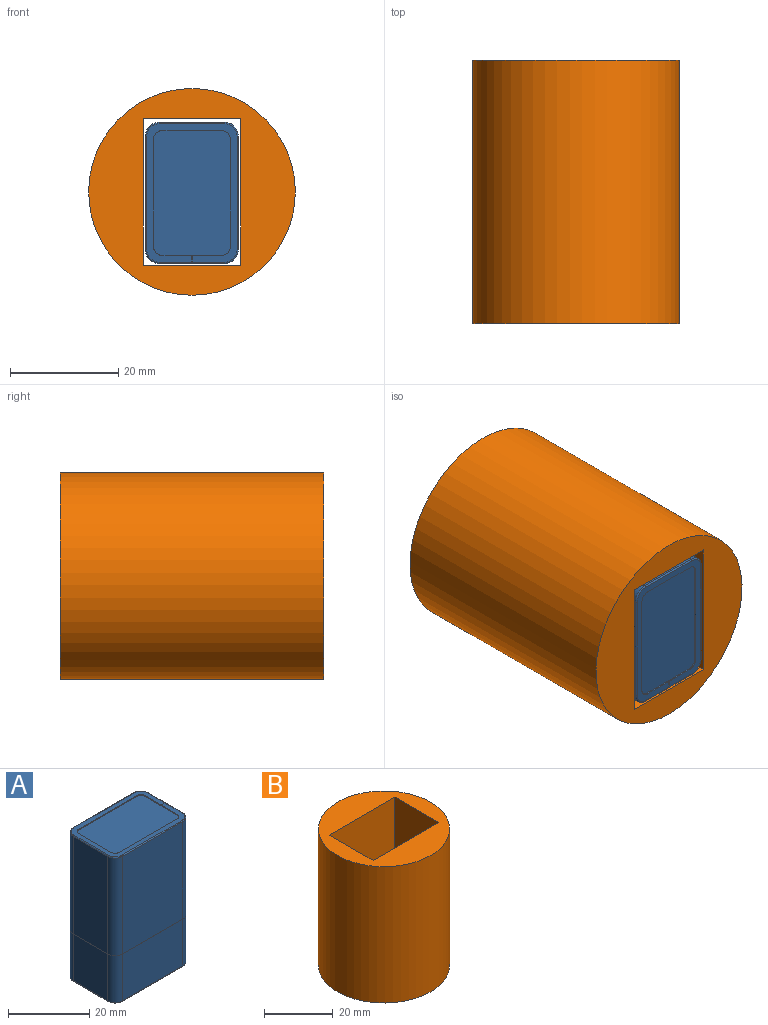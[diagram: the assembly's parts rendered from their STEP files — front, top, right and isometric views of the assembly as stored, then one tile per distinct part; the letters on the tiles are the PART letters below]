
ASSEMBLY  parts=2 mates=1
PART A: 190 faces, bbox 26.5x17.6x47.9 mm
  f0: cylinder r=0.25mm len=20.96mm, axis (1,0,0), area 8.4mm2, adj f1,f7,f9,f48
  f1: torus R=2.29mm, axis (0,0,-1), area 1.5mm2, adj f0,f2,f9,f49
  f2: cylinder r=0.25mm len=12.07mm, axis (0,-1,0), area 4.8mm2, adj f1,f3,f9,f50
  f3: torus R=2.29mm, axis (0,0,-1), area 1.5mm2, adj f2,f4,f9,f51
  f4: cylinder r=0.25mm len=20.96mm, axis (-1,0,0), area 8.4mm2, adj f3,f5,f9,f35
  f5: torus R=2.29mm, axis (0,0,-1), area 1.5mm2, adj f4,f6,f9,f34
  f6: cylinder r=0.25mm len=5.98mm, axis (0,-1,0), area 2.4mm2, adj f5,f9,f32,f33
  f7: torus R=2.29mm, axis (0,0,-1), area 1.5mm2, adj f0,f8,f9,f47
  f8: cylinder r=0.25mm len=5.98mm, axis (0,-1,0), area 2.4mm2, adj f7,f9,f10,f46
  f9: plane 25.53x16.64mm, normal (0,0,1), area 98mm2, adj f0,f1,f2,f3,f4,f5,f6,f7
  f10: plane 29.59x1.52mm, normal (0,1,0), area 7.8mm2, adj f8,f9,f30,f31,f38,f39,f46
  f11: cylinder r=0.25mm len=20.96mm, axis (-1,0,0), area 8.4mm2, adj f12,f14,f26,f75
  f12: torus R=2.29mm, axis (0,0,1), area 1.5mm2, adj f11,f13,f27,f75
  f13: cylinder r=0.25mm len=5.98mm, axis (0,-1,0), area 2.4mm2, adj f12,f28,f29,f75
  f14: torus R=2.29mm, axis (0,0,1), area 1.5mm2, adj f11,f15,f25,f75
  f15: cylinder r=0.25mm len=12.07mm, axis (0,-1,0), area 4.8mm2, adj f14,f16,f24,f75
  f16: torus R=2.29mm, axis (0,0,1), area 1.5mm2, adj f15,f17,f23,f75
  f17: cylinder r=0.25mm len=20.96mm, axis (1,0,0), area 8.4mm2, adj f16,f18,f22,f75
  f18: torus R=2.29mm, axis (0,0,1), area 1.5mm2, adj f17,f19,f21,f75
  f19: cylinder r=0.25mm len=5.98mm, axis (0,-1,0), area 2.4mm2, adj f18,f20,f65,f75
  f20: plane 14.07x5.98mm, normal (1,0,0), area 84.2mm2, adj f19,f21,f64,f65
  f21: cylinder r=2.54mm len=14.07mm, axis (0,0,1), area 56.1mm2, adj f18,f20,f22,f64
  f22: plane 20.96x14.07mm, normal (0,1,0), area 294.9mm2, adj f17,f21,f23,f64
  f23: cylinder r=2.54mm len=14.07mm, axis (0,0,-1), area 56.1mm2, adj f16,f22,f24,f64
  f24: plane 14.07x12.07mm, normal (-1,0,0), area 169.8mm2, adj f15,f23,f25,f64
  f25: cylinder r=2.54mm len=14.07mm, axis (0,0,1), area 56.1mm2, adj f14,f24,f26,f64
  f26: plane 20.96x14.07mm, normal (0,-1,0), area 294.9mm2, adj f11,f25,f27,f64
  f27: cylinder r=2.54mm len=14.07mm, axis (0,0,-1), area 56.1mm2, adj f12,f26,f28,f64
  f28: plane 14.07x5.98mm, normal (1,0,0), area 84.2mm2, adj f13,f27,f29,f64
  f29: plane 14.33x1.52mm, normal (0,1,0), area 3.9mm2, adj f13,f28,f64,f66,f70,f75,f76
  f30: plane 26.04x17.15mm, normal (0,0,-1), area 0.2mm2, adj f10,f31,f32,f33,f34,f35,f46,f47
  f31: plane 29.34x0.1mm, normal (1,0,0), area 3mm2, adj f10,f30,f32,f38
  f32: plane 29.59x1.52mm, normal (0,-1,0), area 7.8mm2, adj f6,f9,f30,f31,f33,f37,f38
  f33: plane 29.34x5.98mm, normal (1,0,0), area 175.5mm2, adj f6,f30,f32,f34
  f34: cylinder r=2.54mm len=29.34mm, axis (0,0,1), area 117mm2, adj f5,f30,f33,f35
  f35: plane 29.34x20.96mm, normal (0,1,0), area 614.8mm2, adj f4,f30,f34,f51
  f36: plane 11.05x0.25mm, normal (1,0,0), area 2.8mm2, adj f9,f38,f40,f41
  f37: plane 5.47x0.25mm, normal (-1,0,0), area 1.4mm2, adj f9,f32,f38,f43
  f38: plane 24.26x14.1mm, normal (0,0,1), area 322.2mm2, adj f10,f31,f32,f36,f37,f39,f40,f41
  f39: plane 5.47x0.25mm, normal (-1,0,0), area 1.4mm2, adj f9,f10,f38,f45
  f40: cylinder r=1.52mm len=1.52mm, axis (0,0,1), area 0.6mm2, adj f9,f36,f38,f44
  f41: cylinder r=1.52mm len=1.52mm, axis (0,0,1), area 0.6mm2, adj f9,f36,f38,f42
  f42: plane 19.94x0.25mm, normal (0,-1,0), area 5.1mm2, adj f9,f38,f41,f43
  f43: cylinder r=1.52mm len=1.52mm, axis (0,0,1), area 0.6mm2, adj f9,f37,f38,f42
  f44: plane 19.94x0.25mm, normal (0,1,0), area 5.1mm2, adj f9,f38,f40,f45
  f45: cylinder r=1.52mm len=1.52mm, axis (0,0,1), area 0.6mm2, adj f9,f38,f39,f44
  f46: plane 29.34x5.98mm, normal (1,0,0), area 175.5mm2, adj f8,f10,f30,f47
  f47: cylinder r=2.54mm len=29.34mm, axis (0,0,-1), area 117mm2, adj f7,f30,f46,f48
  f48: plane 29.34x20.96mm, normal (0,-1,0), area 614.8mm2, adj f0,f30,f47,f49
  f49: cylinder r=2.54mm len=29.34mm, axis (0,0,1), area 117mm2, adj f1,f30,f48,f50
  f50: plane 29.34x12.07mm, normal (-1,0,0), area 354mm2, adj f2,f30,f49,f51
  f51: cylinder r=2.54mm len=29.34mm, axis (0,0,-1), area 117mm2, adj f3,f30,f35,f50
  f52: cylinder r=2.54mm len=2.54mm, axis (0,0,1), area 0.1mm2, adj f30,f53,f57,f64
  f53: plane 20.96x0.03mm, normal (0,1,0), area 0.5mm2, adj f30,f52,f58,f64
  f54: plane 0.25x0.03mm, normal (0,1,0), area 0mm2, adj f30,f55,f63,f64
  f55: plane 0.11x0.03mm, normal (1,0,0), area 0mm2, adj f30,f54,f56,f64
  f56: plane 0.25x0.03mm, normal (0,-1,0), area 0mm2, adj f30,f55,f57,f64
  f57: plane 5.98x0.03mm, normal (1,0,0), area 0.2mm2, adj f30,f52,f56,f64
  f58: cylinder r=2.54mm len=2.54mm, axis (0,0,-1), area 0.1mm2, adj f30,f53,f59,f64
  f59: plane 12.07x0.03mm, normal (-1,0,0), area 0.3mm2, adj f30,f58,f60,f64
  f60: cylinder r=2.54mm len=2.54mm, axis (0,0,1), area 0.1mm2, adj f30,f59,f61,f64
  f61: plane 20.96x0.03mm, normal (0,-1,0), area 0.5mm2, adj f30,f60,f62,f64
  f62: cylinder r=2.54mm len=2.54mm, axis (0,0,-1), area 0.1mm2, adj f30,f61,f63,f64
  f63: plane 5.98x0.03mm, normal (1,0,0), area 0.2mm2, adj f30,f54,f62,f64
  f64: plane 26.04x17.15mm, normal (0,0,1), area 0.2mm2, adj f20,f21,f22,f23,f24,f25,f26,f27
  f65: plane 14.33x1.52mm, normal (0,-1,0), area 3.9mm2, adj f19,f20,f64,f66,f70,f74,f75
  f66: plane 14.07x0.1mm, normal (1,0,0), area 1.4mm2, adj f29,f64,f65,f70
  f67: cylinder r=1.52mm len=1.52mm, axis (0,0,-1), area 0.6mm2, adj f68,f70,f75,f189
  f68: plane 19.94x0.25mm, normal (0,1,0), area 5.1mm2, adj f67,f70,f72,f75
  f69: cylinder r=1.52mm len=1.52mm, axis (0,0,-1), area 0.6mm2, adj f70,f71,f75,f189
  f70: plane 24.26x14.1mm, normal (0,0,-1), area 246.7mm2, adj f29,f65,f66,f67,f68,f69,f71,f72
  f71: plane 19.94x0.25mm, normal (0,-1,0), area 5.1mm2, adj f69,f70,f73,f75
  f72: cylinder r=1.52mm len=1.52mm, axis (0,0,-1), area 0.6mm2, adj f68,f70,f75,f76
  f73: cylinder r=1.52mm len=1.52mm, axis (0,0,-1), area 0.6mm2, adj f70,f71,f74,f75
  f74: plane 5.47x0.25mm, normal (-1,0,0), area 1.4mm2, adj f65,f70,f73,f75
  f75: plane 25.53x16.64mm, normal (0,0,-1), area 98mm2, adj f11,f12,f13,f14,f15,f16,f17,f18
  f76: plane 5.47x0.25mm, normal (-1,0,0), area 1.4mm2, adj f29,f70,f72,f75
  f77: plane 1.08x0.76mm, normal (0,-1,0), area 0.4mm2, adj f110,f140,f141,f142,f145,f148,f161,f162
  f78: cylinder r=0.25mm len=3.21mm, axis (-1,0,0), area 1.3mm2, adj f79,f80,f95,f97
  f79: plane 3.21x0.57mm, normal (0,0,-1), area 1.8mm2, adj f78,f80,f93,f95
  f80: plane 1.08x0.76mm, normal (1,0,0), area 0.4mm2, adj f78,f79,f84,f89,f92,f93,f94,f96
  f81: plane 1.08x0.76mm, normal (0,-1,0), area 0.4mm2, adj f101,f176,f177,f178,f180,f182,f184,f185
  f82: cylinder r=0.13mm len=0.36mm, axis (0,1,0), area 0.1mm2, adj f98,f99,f175,f176
  f83: cylinder r=0.25mm len=0.86mm, axis (0,-1,0), area 0.3mm2, adj f103,f104,f187,f188
  f84: plane 3.32x1.4mm, normal (0,-1,0), area 4.6mm2, adj f80,f85,f90,f91,f93,f95,f101,f102
  f85: cylinder r=0.25mm len=0.86mm, axis (-1,0,0), area 0.3mm2, adj f84,f90,f107,f108
  f86: cylinder r=0.13mm len=0.36mm, axis (-1,0,0), area 0.1mm2, adj f87,f89,f112,f113
  f87: bspline ~2.49x0.15mm, area 0.4mm2, adj f86,f88,f89,f172
  f88: cylinder r=0.13mm len=0.36mm, axis (1,0,0), area 0.1mm2, adj f87,f89,f98,f99
  f89: plane 3.21x1.3mm, normal (0,1,0), area 4.1mm2, adj f80,f86,f87,f88,f92,f95,f100,f111
  f90: bspline ~1.77x0.27mm, area 0.6mm2, adj f84,f85,f91,f179
  f91: cylinder r=0.25mm len=0.86mm, axis (-1,0,0), area 0.3mm2, adj f84,f90,f103,f104
  f92: plane 3.21x0.57mm, normal (0,0,1), area 1.8mm2, adj f80,f89,f94,f95
  f93: cylinder r=0.25mm len=3.21mm, axis (1,0,0), area 1.3mm2, adj f79,f80,f84,f95
  f94: plane 3.21x0.51mm, normal (0,-1,0), area 1.6mm2, adj f80,f92,f95,f96
  f95: plane 1.08x0.76mm, normal (-1,0,0), area 0.4mm2, adj f78,f79,f84,f89,f92,f93,f94,f96
  f96: plane 3.21x0.25mm, normal (0,0,1), area 0.8mm2, adj f80,f94,f95,f97
  f97: plane 3.21x0.51mm, normal (0,1,0), area 1.6mm2, adj f78,f80,f95,f96
  f98: plane 2.22x2.22mm, normal (0,0,-1), area 0.4mm2, adj f82,f88,f99,f172
  f99: torus R=3.81mm, axis (0,0,-1), area 0.6mm2, adj f82,f88,f98,f100
  f100: cylinder r=3.94mm len=1.99mm, axis (0,0,-1), area 3.3mm2, adj f89,f99,f101,f176
  f101: plane 2.24x2.24mm, normal (0,0,-1), area 0.8mm2, adj f80,f81,f84,f100,f102,f187
  f102: cylinder r=4.19mm len=2.19mm, axis (0,0,-1), area 4mm2, adj f84,f101,f103,f187
  f103: torus R=3.94mm, axis (0,0,1), area 1.2mm2, adj f83,f91,f102,f104
  f104: plane 2.79x2.79mm, normal (0,0,1), area 0.9mm2, adj f83,f91,f103,f179
  f105: cylinder r=0.25mm len=0.86mm, axis (0,1,0), area 0.3mm2, adj f107,f108,f146,f148
  f106: cylinder r=0.13mm len=0.36mm, axis (0,1,0), area 0.1mm2, adj f112,f113,f145,f171
  f107: plane 2.79x2.79mm, normal (0,0,1), area 0.9mm2, adj f85,f105,f108,f179
  f108: torus R=3.94mm, axis (0,0,1), area 1.2mm2, adj f85,f105,f107,f109
  f109: cylinder r=4.19mm len=2.19mm, axis (0,0,-1), area 4mm2, adj f84,f108,f110,f148
  f110: plane 2.24x2.24mm, normal (0,0,-1), area 0.8mm2, adj f77,f84,f95,f109,f111,f148
  f111: cylinder r=3.94mm len=1.99mm, axis (0,0,-1), area 3.3mm2, adj f89,f110,f112,f145
  f112: torus R=3.81mm, axis (0,0,1), area 0.6mm2, adj f86,f106,f111,f113
  f113: plane 2.22x2.22mm, normal (0,0,-1), area 0.4mm2, adj f86,f106,f112,f172
  f114: plane 3.21x0.57mm, normal (0,0,-1), area 1.8mm2, adj f125,f129,f167,f168
  f115: torus R=3.94mm, axis (0,0,1), area 1.2mm2, adj f116,f124,f138,f147
  f116: plane 2.79x2.79mm, normal (0,0,1), area 0.9mm2, adj f115,f138,f147,f179
  f117: plane 2.79x2.79mm, normal (0,0,1), area 0.9mm2, adj f118,f134,f164,f179
  f118: torus R=3.94mm, axis (0,0,1), area 1.2mm2, adj f117,f119,f134,f164
  f119: cylinder r=4.19mm len=2.19mm, axis (0,0,-1), area 4mm2, adj f118,f127,f139,f187
  f120: plane 2.22x2.22mm, normal (0,0,-1), area 0.4mm2, adj f121,f137,f144,f172
  f121: torus R=3.81mm, axis (0,0,1), area 0.6mm2, adj f120,f122,f137,f144
  f122: cylinder r=3.94mm len=1.99mm, axis (0,0,-1), area 3.3mm2, adj f121,f123,f132,f145
  f123: plane 2.24x2.24mm, normal (0,0,-1), area 0.8mm2, adj f122,f124,f139,f143,f148,f167
  f124: cylinder r=4.19mm len=2.19mm, axis (0,0,-1), area 4mm2, adj f115,f123,f139,f148
  f125: cylinder r=0.25mm len=3.21mm, axis (-1,0,0), area 1.3mm2, adj f114,f129,f139,f167
  f126: plane 3.21x0.57mm, normal (0,0,1), area 1.8mm2, adj f129,f132,f160,f167
  f127: plane 2.24x2.24mm, normal (0,0,-1), area 0.8mm2, adj f119,f128,f129,f139,f165,f187
  f128: cylinder r=3.94mm len=1.99mm, axis (0,0,-1), area 3.3mm2, adj f127,f131,f132,f176
  f129: plane 1.08x0.76mm, normal (1,0,0), area 0.4mm2, adj f114,f125,f126,f127,f132,f139,f159,f160
  f130: plane 2.22x2.22mm, normal (0,0,-1), area 0.4mm2, adj f131,f135,f163,f172
  f131: torus R=3.81mm, axis (0,0,-1), area 0.6mm2, adj f128,f130,f135,f163
  f132: plane 3.21x1.3mm, normal (0,-1,0), area 4.1mm2, adj f122,f126,f128,f129,f135,f136,f137,f167
  f133: bspline ~1.77x0.27mm, area 0.6mm2, adj f134,f138,f139,f179
  f134: cylinder r=0.25mm len=0.86mm, axis (1,0,0), area 0.3mm2, adj f117,f118,f133,f139
  f135: cylinder r=0.13mm len=0.36mm, axis (-1,0,0), area 0.1mm2, adj f130,f131,f132,f136
  f136: bspline ~2.49x0.15mm, area 0.4mm2, adj f132,f135,f137,f172
  f137: cylinder r=0.13mm len=0.36mm, axis (1,0,0), area 0.1mm2, adj f120,f121,f132,f136
  f138: cylinder r=0.25mm len=0.86mm, axis (1,0,0), area 0.3mm2, adj f115,f116,f133,f139
  f139: plane 3.32x1.4mm, normal (0,1,0), area 4.6mm2, adj f119,f123,f124,f125,f127,f129,f133,f134
  f140: plane 3.21x0.57mm, normal (0,0,-1), area 1.8mm2, adj f77,f141,f143,f170
  f141: cylinder r=0.25mm len=3.21mm, axis (0,-1,0), area 1.3mm2, adj f77,f140,f143,f148
  f142: plane 3.21x0.57mm, normal (0,0,1), area 1.8mm2, adj f77,f143,f145,f162
  f143: plane 1.08x0.76mm, normal (0,1,0), area 0.4mm2, adj f123,f140,f141,f142,f145,f148,f161,f162
  f144: cylinder r=0.13mm len=0.36mm, axis (0,1,0), area 0.1mm2, adj f120,f121,f145,f171
  f145: plane 3.21x1.3mm, normal (1,0,0), area 4.1mm2, adj f77,f106,f111,f122,f142,f143,f144,f171
  f146: bspline ~1.77x0.27mm, area 0.6mm2, adj f105,f147,f148,f179
  f147: cylinder r=0.25mm len=0.86mm, axis (0,1,0), area 0.3mm2, adj f115,f116,f146,f148
  f148: plane 3.32x1.4mm, normal (-1,0,0), area 4.6mm2, adj f77,f105,f109,f110,f123,f124,f141,f143
  f149: torus R=2.29mm, axis (0,0,1), area 5.3mm2, adj f150,f152
  f150: plane 5.21x5.21mm, normal (0,0,-1), area 4.9mm2, adj f149,f151
  f151: torus R=2.6mm, axis (0,0,1), area 6.9mm2, adj f150,f156
  f152: cylinder r=2.03mm len=4.06mm, axis (0,0,-1), area 38.9mm2, adj f149,f155
  f153: cylinder r=3.94mm len=7.87mm, axis (0,0,1), area 3.1mm2, adj f70,f154
  f154: plane 7.87x7.87mm, normal (0,0,-1), area 25.6mm2, adj f153,f157
  f155: plane 4.06x4.06mm, normal (0,0,-1), area 13mm2, adj f152
  f156: cylinder r=2.86mm len=5.72mm, axis (0,0,1), area 27.2mm2, adj f151,f158
  f157: cone r=2.83mm half-angle=6deg, axis (0,0,-1), area 22.2mm2, adj f154,f158
  f158: torus R=0.32mm, axis (0,0,1), area 4.8mm2, adj f156,f157
  f159: plane 3.21x0.25mm, normal (0,0,1), area 0.8mm2, adj f129,f160,f166,f167
  f160: plane 3.21x0.51mm, normal (0,1,0), area 1.6mm2, adj f126,f129,f159,f167
  f161: plane 3.21x0.25mm, normal (0,0,1), area 0.8mm2, adj f77,f143,f162,f169
  f162: plane 3.21x0.51mm, normal (-1,0,0), area 1.6mm2, adj f77,f142,f143,f161
  f163: cylinder r=0.13mm len=0.36mm, axis (0,1,0), area 0.1mm2, adj f130,f131,f175,f176
  f164: cylinder r=0.25mm len=0.86mm, axis (0,-1,0), area 0.3mm2, adj f117,f118,f187,f188
  f165: plane 1.08x0.76mm, normal (0,1,0), area 0.4mm2, adj f127,f176,f177,f178,f180,f182,f184,f185
  f166: plane 3.21x0.51mm, normal (0,-1,0), area 1.6mm2, adj f129,f159,f167,f168
  f167: plane 1.08x0.76mm, normal (-1,0,0), area 0.4mm2, adj f114,f123,f125,f126,f132,f139,f159,f160
  f168: cylinder r=0.25mm len=3.21mm, axis (1,0,0), area 1.3mm2, adj f114,f129,f166,f167
  f169: plane 3.21x0.51mm, normal (1,0,0), area 1.6mm2, adj f77,f143,f161,f170
  f170: cylinder r=0.25mm len=3.21mm, axis (0,1,0), area 1.3mm2, adj f77,f140,f143,f169
  f171: bspline ~2.49x0.15mm, area 0.4mm2, adj f106,f144,f145,f172
  f172: torus R=3.68mm, axis (0,0,1), area 22.9mm2, adj f87,f98,f113,f120,f130,f136,f171,f173
  f173: cylinder r=2.92mm len=5.84mm, axis (0,0,-1), area 28mm2, adj f172,f174
  f174: plane 5.84x5.84mm, normal (0,0,-1), area 26.8mm2, adj f173
  f175: bspline ~2.49x0.15mm, area 0.4mm2, adj f82,f163,f172,f176
  f176: plane 3.21x1.3mm, normal (-1,0,0), area 4.1mm2, adj f81,f82,f100,f128,f163,f165,f175,f177
  f177: plane 3.21x0.57mm, normal (0,0,1), area 1.8mm2, adj f81,f165,f176,f178
  f178: plane 3.21x0.51mm, normal (1,0,0), area 1.6mm2, adj f81,f165,f177,f180
  f179: torus R=3.68mm, axis (0,0,1), area 16.6mm2, adj f90,f104,f107,f116,f117,f133,f146,f181
  f180: plane 3.21x0.25mm, normal (0,0,1), area 0.8mm2, adj f81,f165,f178,f182
  f181: cylinder r=3.17mm len=6.35mm, axis (0,0,-1), area 30.4mm2, adj f179,f183
  f182: plane 3.21x0.51mm, normal (-1,0,0), area 1.6mm2, adj f81,f165,f180,f184
  f183: torus R=2.92mm, axis (0,0,1), area 7.7mm2, adj f70,f181
  f184: cylinder r=0.25mm len=3.21mm, axis (0,-1,0), area 1.3mm2, adj f81,f165,f182,f185
  f185: plane 3.21x0.57mm, normal (0,0,-1), area 1.8mm2, adj f81,f165,f184,f186
  f186: cylinder r=0.25mm len=3.21mm, axis (0,1,0), area 1.3mm2, adj f81,f165,f185,f187
  f187: plane 3.32x1.4mm, normal (1,0,0), area 4.6mm2, adj f81,f83,f101,f102,f119,f127,f164,f165
  f188: bspline ~1.77x0.27mm, area 0.6mm2, adj f83,f164,f179,f187
  f189: plane 11.05x0.25mm, normal (1,0,0), area 2.8mm2, adj f67,f69,f70,f75
PART B: 7 faces, bbox 38.1x38.1x48.5 mm
  f0: plane 48.5x18mm, normal (-1,0,0), area 873mm2, adj f1,f3,f5,f6
  f1: plane 48.5x27mm, normal (0,1,0), area 1309.5mm2, adj f0,f2,f5,f6
  f2: plane 48.5x18mm, normal (1,0,0), area 873mm2, adj f1,f3,f5,f6
  f3: plane 48.5x27mm, normal (0,-1,0), area 1309.5mm2, adj f0,f2,f5,f6
  f4: cylinder r=19.05mm len=48.5mm, axis (0,0,-1), area 5805.2mm2, adj f5,f6
  f5: plane 38.1x38.1mm, normal (0,0,1), area 654.1mm2, adj f0,f1,f2,f3,f4
  f6: plane 38.1x38.1mm, normal (0,0,-1), area 654.1mm2, adj f0,f1,f2,f3,f4
PLACE A rot(axis=(0.58,0.58,-0.58),120deg) t=(-32.43,59.6,-3.89)mm
PLACE B rot(axis=(0.58,0.58,-0.58),120deg) t=(-40.98,18.9,16.41)mm
MATE planar A.f9 <-> B.f4  axis (0,-1,0) through (-47.03,-29.6,28.98)mm
